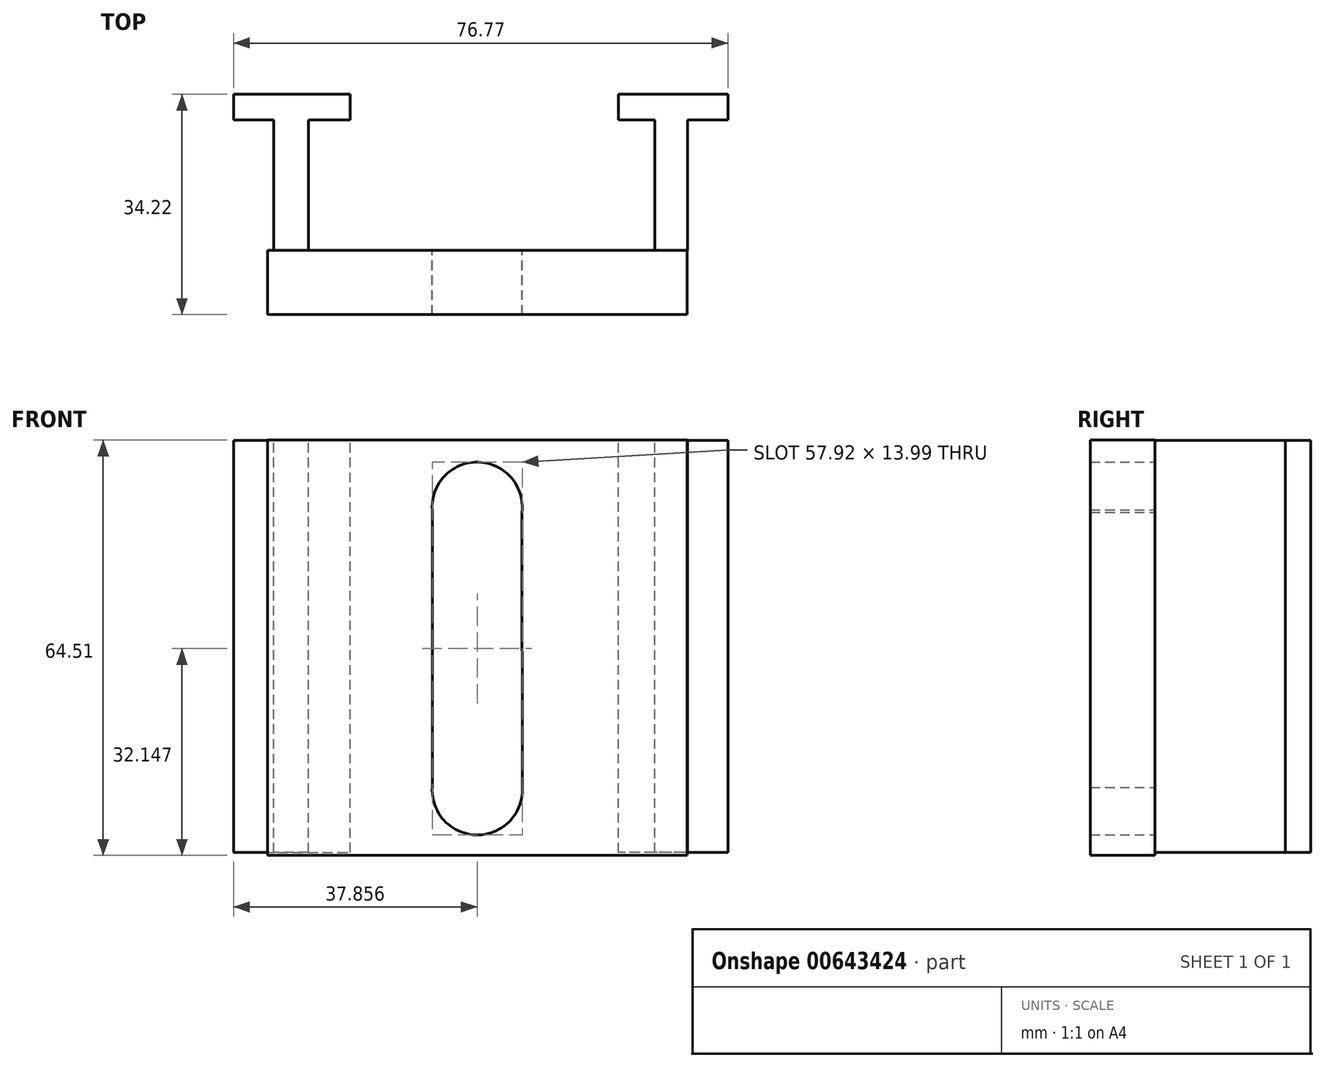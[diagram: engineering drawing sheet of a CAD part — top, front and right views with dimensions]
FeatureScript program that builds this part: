
annotation { "Feature Type Name" : "Feature", "Feature Type Description" : "" }
export const myFeature = defineFeature(function(context is Context, id is Id, definition is map)
    precondition{}
    {
        {
            var Q0;
            Q0=qCreatedBy(makeId("Front.planeOp"),FACE);
            var sketch = newSketch(context, id + "F0", { "sketchPlane" : qUnion([Q0])});
            skLineSegment(sketch, "E0.bottom", {"start": v(-30.84, 21.03) * mm, "end": v(34.3, 21.03) * mm});
            skLineSegment(sketch, "E0.top", {"start": v(-30.84, -43.48) * mm, "end": v(34.3, -43.48) * mm});
            skLineSegment(sketch, "E0.left", {"start": v(-30.84, 21.03) * mm, "end": v(-30.84, -43.48) * mm});
            skLineSegment(sketch, "E0.right", {"start": v(34.3, 21.03) * mm, "end": v(34.3, -43.48) * mm});
            skArc(sketch, "E1", {"start": v(8.68, 9.83) * mm, "mid": v(1.93, 17.63) * mm, "end": v(-5.26, 10.22) * mm});
            skPoint(sketch, "E1.centerSnap0", {"position": v(1.73, 21.03) * mm});
            skArc(sketch, "E2", {"start": v(-5.26, -32.89) * mm, "mid": v(1.53, -40.3) * mm, "end": v(8.73, -33.29) * mm});
            skLineSegment(sketch, "E3", {"start": v(8.68, 11.44) * mm, "end": v(8.73, -33.29) * mm});
            skLineSegment(sketch, "E4", {"start": v(-5.26, 11.03) * mm, "end": v(-5.26, -33.7) * mm});
            skSolve(sketch);
        }
        {
            var Q0;
            Q0=makeQuery(id+"F0.imprint","IMPRINT",FACE,{"disambiguationData":[TD([[makeQuery(id+"F0.imprint","IMPRINT",EDGE,{"derivedFrom":sQuery(id+"F0.wireOp",EDGE,"E0.bottom")}),-1.0]])]});
            extrude(context, id + "F1", {"entities" : qUnion([Q0]), "depth" : 10 * mm, "offsetDistance" : 25 * mm});
        }
        {
            var Q0;
            Q0=qCreatedBy(makeId("Top.planeOp"),FACE);
            var sketch = newSketch(context, id + "F2", { "sketchPlane" : qUnion([Q0])});
            skLineSegment(sketch, "E5.bottom", {"start": v(-24.5, 0) * mm, "end": v(-29.89, 0) * mm});
            skLineSegment(sketch, "E5.left", {"start": v(-24.5, 0) * mm, "end": v(-24.5, 20.25) * mm});
            skLineSegment(sketch, "E5.right", {"start": v(-29.89, 0) * mm, "end": v(-29.89, 20.25) * mm});
            skLineSegment(sketch, "E6.bottom", {"start": v(34.42, 0) * mm, "end": v(29.32, 0) * mm});
            skLineSegment(sketch, "E6.left", {"start": v(34.42, 0) * mm, "end": v(34.42, 20.25) * mm});
            skLineSegment(sketch, "E6.right", {"start": v(29.32, 0) * mm, "end": v(29.32, 20.25) * mm});
            skLineSegment(sketch, "E7.bottom", {"start": v(-36.12, 20.25) * mm, "end": v(-29.89, 20.25) * mm});
            skLineSegment(sketch, "E7.top", {"start": v(-36.12, 24.22) * mm, "end": v(-17.99, 24.22) * mm});
            skLineSegment(sketch, "E7.left", {"start": v(-36.12, 20.25) * mm, "end": v(-36.12, 24.22) * mm});
            skLineSegment(sketch, "E7.right", {"start": v(-17.99, 20.25) * mm, "end": v(-17.99, 24.22) * mm});
            skLineSegment(sketch, "E8.bottom", {"start": v(40.65, 20.25) * mm, "end": v(34.42, 20.25) * mm});
            skLineSegment(sketch, "E8.top", {"start": v(40.65, 24.22) * mm, "end": v(23.65, 24.22) * mm});
            skLineSegment(sketch, "E8.left", {"start": v(40.65, 20.25) * mm, "end": v(40.65, 24.22) * mm});
            skLineSegment(sketch, "E8.right", {"start": v(23.65, 20.25) * mm, "end": v(23.65, 24.22) * mm});
            skLineSegment(sketch, "E9.trimOffspring", {"start": v(29.32, 20.25) * mm, "end": v(23.65, 20.25) * mm});
            skLineSegment(sketch, "E10.trimOffspring", {"start": v(-24.5, 20.25) * mm, "end": v(-17.99, 20.25) * mm});
            skSolve(sketch);
        }
        {
            var Q0;
            Q0=makeQuery(id+"F2.imprint","IMPRINT",FACE,{"disambiguationData":[TD([[makeQuery(id+"F2.imprint","IMPRINT",EDGE,{"derivedFrom":sQuery(id+"F2.wireOp",EDGE,"E5.bottom")}),-1.0]])]});
            var Q1;
            Q1=makeQuery(id+"F2.imprint","IMPRINT",FACE,{"disambiguationData":[TD([[makeQuery(id+"F2.imprint","IMPRINT",EDGE,{"derivedFrom":sQuery(id+"F2.wireOp",EDGE,"E6.bottom")}),-1.0]])]});
            extrude(context, id + "F3", {"entities" : qUnion([Q0, Q1]), "operationType" : NewBodyOperationType.ADD, "oppositeDirection" : true, "depth" : 43 * mm, "offsetDistance" : 25 * mm});
        }
        {
            var Q0;
            Q0=makeQuery(id+"F3.opExtrude","CAP_FACE",FACE,{"disambiguationData":[OSD([sQuery(id+"F2.wireOp",EDGE,"E6.bottom"),sQuery(id+"F2.wireOp",EDGE,"E6.left"),sQuery(id+"F2.wireOp",EDGE,"E6.right"),sQuery(id+"F2.wireOp",EDGE,"E8.bottom"),sQuery(id+"F2.wireOp",EDGE,"E8.top"),sQuery(id+"F2.wireOp",EDGE,"E8.left"),sQuery(id+"F2.wireOp",EDGE,"E8.right"),sQuery(id+"F2.wireOp",EDGE,"E9.trimOffspring")])],"isStart":true});
            var Q1;
            Q1=makeQuery(id+"F3.opExtrude","CAP_FACE",FACE,{"disambiguationData":[OSD([sQuery(id+"F2.wireOp",EDGE,"E5.bottom"),sQuery(id+"F2.wireOp",EDGE,"E5.left"),sQuery(id+"F2.wireOp",EDGE,"E5.right"),sQuery(id+"F2.wireOp",EDGE,"E7.bottom"),sQuery(id+"F2.wireOp",EDGE,"E7.top"),sQuery(id+"F2.wireOp",EDGE,"E7.left"),sQuery(id+"F2.wireOp",EDGE,"E7.right"),sQuery(id+"F2.wireOp",EDGE,"E10.trimOffspring")])],"isStart":true});
            extrude(context, id + "F4", {"entities" : qUnion([Q0, Q1]), "operationType" : NewBodyOperationType.ADD, "depth" : 21 * mm, "offsetDistance" : 25 * mm});
        }
    });
